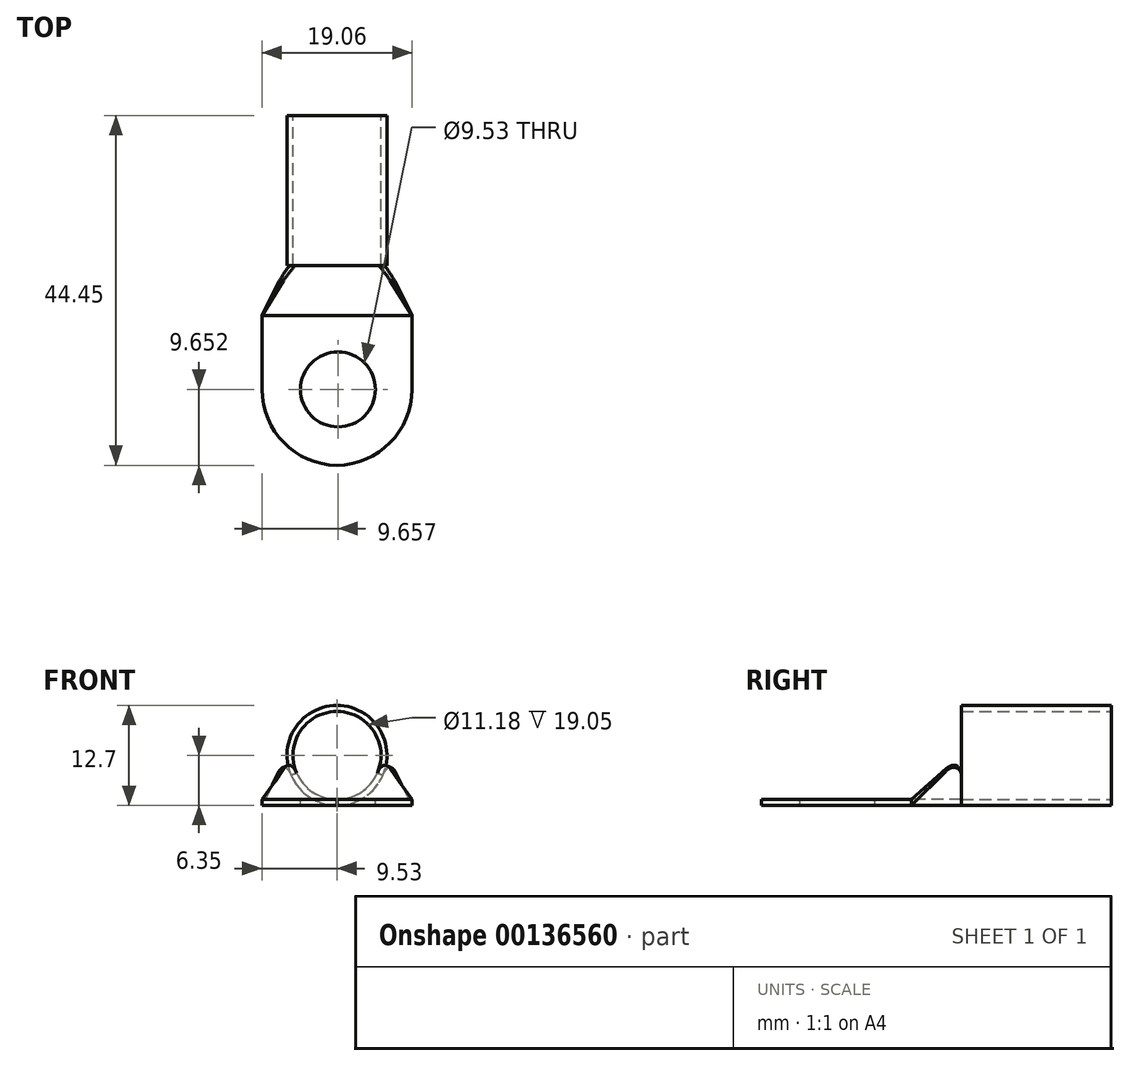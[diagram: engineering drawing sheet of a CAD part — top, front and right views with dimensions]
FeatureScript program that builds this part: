
annotation { "Feature Type Name" : "Feature", "Feature Type Description" : "" }
export const myFeature = defineFeature(function(context is Context, id is Id, definition is map)
    precondition{}
    {
        {
            var Q0;
            Q0=qCreatedBy(makeId("Front.planeOp"),FACE);
            var sketch = newSketch(context, id + "F0", { "sketchPlane" : qUnion([Q0])});
            skCircle(sketch, "E0", {"center": v(0, 0) * mm, "radius": 6.35 * mm});
            skCircle(sketch, "E1", {"center": v(0, 0) * mm, "radius": 5.59 * mm});
            skSolve(sketch);
        }
        {
            var Q0;
            Q0 = qSketchRegion(id + "F0", true);
            extrude(context, id + "F1", {"entities" : qUnion([Q0]), "depth" : 19.05 * mm});
        }
        {
            var Q0;
            Q0=qCreatedBy(makeId("Front.planeOp"),FACE);
            cPlane(context, id + "F2", {"entities" : qUnion([Q0]), "cplaneType" : CPlaneType.OFFSET, "offset" : 50.8 * mm, "width" : 152.4 * mm, "height" : 152.4 * mm});
        }
        {
            var Q0;
            Q0=makeQuery(id+"F1.opExtrude","CAP_FACE",FACE,{"disambiguationData":[OSD([sQuery(id+"F0.wireOp",EDGE,"E0"),sQuery(id+"F0.wireOp",EDGE,"E1")])],"isStart":false});
            var sketch = newSketch(context, id + "F3", { "sketchPlane" : qUnion([Q0])});
            skArc(sketch, "E2.0", {"start": v(-5.59, 0) * mm, "mid": v(0, -5.59) * mm, "end": v(5.59, 0) * mm});
            skArc(sketch, "E2.1", {"start": v(-6.35, 0) * mm, "mid": v(0, -6.35) * mm, "end": v(6.35, 0) * mm});
            skLineSegment(sketch, "E3", {"start": v(-6.35, 0) * mm, "end": v(-5.59, 0) * mm});
            skLineSegment(sketch, "E4", {"start": v(5.59, 0) * mm, "end": v(6.35, 0) * mm});
            skSolve(sketch);
        }
        {
            var Q0;
            Q0=qCreatedBy(makeId("Front.planeOp"),FACE);
            cPlane(context, id + "F4", {"entities" : qUnion([Q0]), "cplaneType" : CPlaneType.OFFSET, "offset" : 25.4 * mm, "width" : 152.4 * mm, "height" : 152.4 * mm});
        }
        {
            var Q0;
            Q0=qCreatedBy(id+"F4.planeOp",FACE);
            var sketch = newSketch(context, id + "F5", { "sketchPlane" : qUnion([Q0])});
            skLineSegment(sketch, "E5.bottom", {"start": v(9.53, -5.59) * mm, "end": v(-9.53, -5.59) * mm});
            skLineSegment(sketch, "E5.top", {"start": v(9.53, -6.35) * mm, "end": v(-9.53, -6.35) * mm});
            skLineSegment(sketch, "E5.left", {"start": v(9.53, -5.59) * mm, "end": v(9.53, -6.35) * mm});
            skLineSegment(sketch, "E5.right", {"start": v(-9.53, -5.59) * mm, "end": v(-9.53, -6.35) * mm});
            skPoint(sketch, "E5.middle", {"position": v(0, -5.97) * mm});
            skSolve(sketch);
        }
        {
            var Q0;
            Q0 = qSketchRegion(id + "F3", true);
            var Q1;
            Q1 = qSketchRegion(id + "F5", true);
            loft(context, id + "F6", {"sheetProfilesArray" : [{ "sheetProfileEntities" : qUnion([Q0]) }, { "sheetProfileEntities" : qUnion([Q1]) }]});
        }
        {
            var Q0;
            Q0=makeQuery(id+"F6.opLoft","CAP_FACE",FACE,{"disambiguationData":[OSD([makeQuery(id+"F5.imprint","IMPRINT",FACE,{"disambiguationData":[TD([[makeQuery(id+"F5.imprint","IMPRINT",EDGE,{"derivedFrom":sQuery(id+"F5.wireOp",EDGE,"E5.bottom")}),1.0]])]})])],"isStart":true});
            extrude(context, id + "F7", {"entities" : qUnion([Q0]), "operationType" : NewBodyOperationType.ADD, "depth" : 19.05 * mm});
        }
        {
            var Q0;
            Q0=makeQuery(id+"F7.opExtrude","CAP_EDGE",EDGE,{"disambiguationData":[OSD([sQuery(id+"F5.wireOp",EDGE,"E5.bottom"),sQuery(id+"F5.wireOp",EDGE,"E5.top"),sQuery(id+"F5.wireOp",EDGE,"E5.left")])],"isStart":false});
            var Q1;
            Q1=makeQuery(id+"F7.opExtrude","CAP_EDGE",EDGE,{"disambiguationData":[OSD([sQuery(id+"F5.wireOp",EDGE,"E5.bottom"),sQuery(id+"F5.wireOp",EDGE,"E5.top"),sQuery(id+"F5.wireOp",EDGE,"E5.right")])],"isStart":false});
            fillet(context, id + "F8", {"entities" : qUnion([Q0, Q1]), "radius" : 9.65 * mm, "tangentPropagation" : true, "allowEdgeOverflow" : false});
        }
        {
            var Q0;
            Q0=makeQuery(id+"F6.opLoft","MID_CAP_EDGE",EDGE,{"disambiguationData":[OSD([sQuery(id+"F0.wireOp",EDGE,"E0"),sQuery(id+"F0.wireOp",EDGE,"E1"),sQuery(id+"F3.wireOp",EDGE,"E2.0"),sQuery(id+"F3.wireOp",EDGE,"E2.1"),sQuery(id+"F3.wireOp",EDGE,"E4")])],"capPos":0.0});
            var Q1;
            Q1=makeQuery(id+"F6.opLoft","MID_CAP_EDGE",EDGE,{"disambiguationData":[OSD([sQuery(id+"F0.wireOp",EDGE,"E0"),sQuery(id+"F0.wireOp",EDGE,"E1"),sQuery(id+"F3.wireOp",EDGE,"E2.0"),sQuery(id+"F3.wireOp",EDGE,"E2.1"),sQuery(id+"F3.wireOp",EDGE,"E3")])],"capPos":0.0});
            fillet(context, id + "F9", {"entities" : qUnion([Q0, Q1]), "radius" : 1.27 * mm, "tangentPropagation" : true, "allowEdgeOverflow" : false});
        }
        {
            var Q0;
            Q0=makeQuery(id+"F7.opExtrude","SWEPT_FACE",FACE,{"disambiguationData":[OSD([sQuery(id+"F5.wireOp",EDGE,"E5.bottom"),sQuery(id+"F5.wireOp",EDGE,"E5.left"),sQuery(id+"F5.wireOp",EDGE,"E5.right")])]});
            var sketch = newSketch(context, id + "F10", { "sketchPlane" : qUnion([Q0])});
            skCircle(sketch, "E6", {"center": v(0.13, -34.8) * mm, "radius": 4.76 * mm});
            skSolve(sketch);
        }
        {
            var Q0;
            Q0 = qSketchRegion(id + "F10", true);
            extrude(context, id + "F11", {"entities" : qUnion([Q0]), "operationType" : NewBodyOperationType.REMOVE, "oppositeDirection" : true, "depth" : 25.4 * mm});
        }
    });
